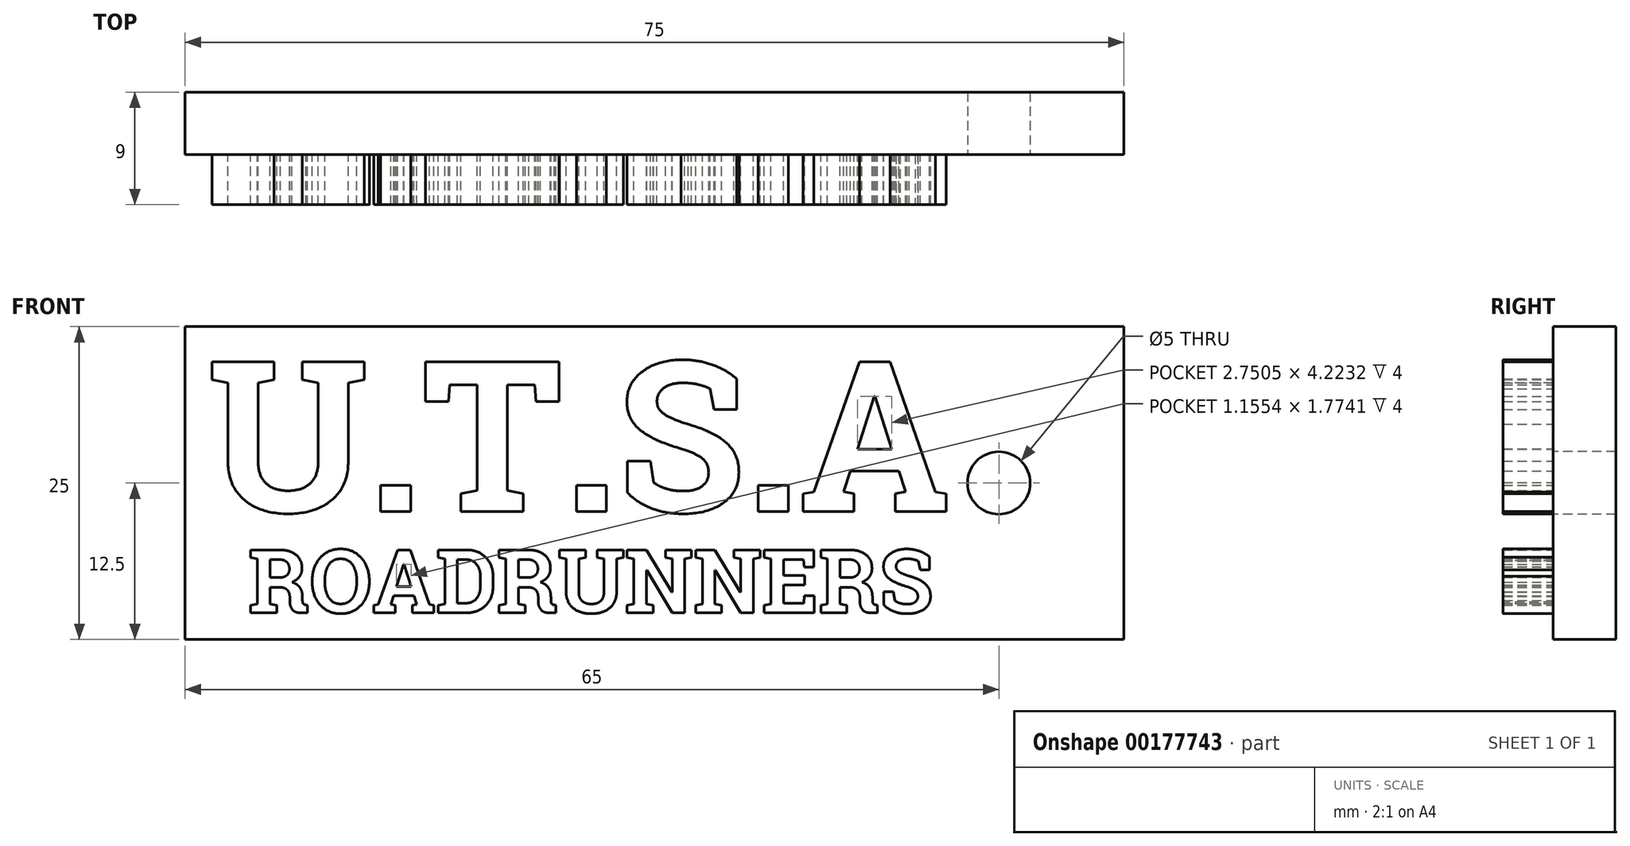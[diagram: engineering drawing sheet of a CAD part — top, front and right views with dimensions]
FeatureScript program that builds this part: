
annotation { "Feature Type Name" : "Feature", "Feature Type Description" : "" }
export const myFeature = defineFeature(function(context is Context, id is Id, definition is map)
    precondition{}
    {
        {
            var Q0;
            Q0=qCreatedBy(makeId("Front.planeOp"),FACE);
            var sketch = newSketch(context, id + "F0", { "sketchPlane" : qUnion([Q0])});
            skLineSegment(sketch, "E0.bottom", {"start": v(0, 0) * mm, "end": v(75, 0) * mm});
            skLineSegment(sketch, "E0.top", {"start": v(0, -25) * mm, "end": v(75, -25) * mm});
            skLineSegment(sketch, "E0.left", {"start": v(0, 0) * mm, "end": v(0, -25) * mm});
            skLineSegment(sketch, "E0.right", {"start": v(75, 0) * mm, "end": v(75, -25) * mm});
            skCircle(sketch, "E1", {"center": v(65, -12.5) * mm, "radius": 2.5 * mm});
            skSolve(sketch);
        }
        {
            var Q0;
            Q0=makeQuery(id+"F0.imprint","IMPRINT",FACE,{"disambiguationData":[TD([[makeQuery(id+"F0.imprint","IMPRINT",EDGE,{"derivedFrom":sQuery(id+"F0.wireOp",EDGE,"E0.bottom")}),-1.0]])]});
            var sketch = newSketch(context, id + "F1", { "sketchPlane" : qUnion([Q0])});
            skText(sketch, "E2", { "text": "U.T.S.A", "fontName": "RobotoSlab-Bold.ttf"});
            skText(sketch, "E3", { "text": "ROADRUNNERS", "fontName": "RobotoSlab-Bold.ttf"});
            const initialGuessF1  = {"E2": [0.00183, -0.01479, 1, 0, 0.01214], "E3": [0.00505, -0.02288, 1, 0, 0.0051]};
            skSetInitialGuess(sketch, initialGuessF1);
            skSolve(sketch);
        }
        {
            var Q0;
            Q0=makeQuery(id+"F0.imprint","IMPRINT",FACE,{"disambiguationData":[TD([[makeQuery(id+"F0.imprint","IMPRINT",EDGE,{"derivedFrom":sQuery(id+"F0.wireOp",EDGE,"E0.bottom")}),-1.0]])]});
            extrude(context, id + "F2", {"entities" : qUnion([Q0]), "oppositeDirection" : true, "depth" : 5 * mm});
        }
        {
            var Q0;
            Q0 = qSketchRegion(id + "F1", true);
            extrude(context, id + "F3", {"entities" : qUnion([Q0]), "operationType" : NewBodyOperationType.ADD, "depth" : 4 * mm});
        }
    });
